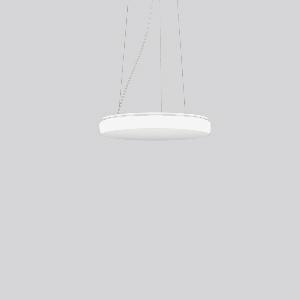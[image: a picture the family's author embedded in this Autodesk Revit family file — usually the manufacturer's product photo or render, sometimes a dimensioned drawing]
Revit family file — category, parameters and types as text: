
# Revit family: flat_polymero_kreis_slim_312090_002_4_76_7d1d
name_source: partatom
category: Lighting Fixtures
units: mm (PartAtom-declared; Revit-internal decimal feet)

## family parameters
Cut with Voids When Loaded = No
Host = Face
Light Source = No
Part Type = Normal
Room Calculation Point = No
Round Connector Dimension = Use Diameter
Shared = No

## types (1)
- FLAT POLYMERO KREIS SLIM (1 x LED Modul 840, 2200 lm, 4000)
    Apparent Load = 19 VA
    CIE Flux Codes = 44 75 94 92 100
    Color Rendering = 80
    Color Temperature = 4000
    Default Elevation = 1800 mm
    Description = Series: FLAT POLYMERO KREIS SLIM
Decorative round LED pendant luminaire. Base and canopy: metal, powder-coated, white. Canopy Ø 205 mm, h 35 mm. Diffuser made of plastic (polycarbonate), opal, shockproof. Diffuser fastening: patented push system. Homogeneous and smooth light distribution. Suitable for pendant. 3-point steel cable suspension, steplessly adjustable. Special lengths available on request. TouchDim sensor capable. Light and/or presence sensors can be integrated. 
Colour: white
Diameter: 460 mm
Height: 68 mm
Suspension length: 200-1300 mm
Lamp: LED
Socket: without socket
Colour temperature: 4000K
Colour rendering index (CRI): 80
System power: 19 W
Rated luminous flux: 2200 lm
Luminous efficiency: 116 lm/W
Control gear: AC power, DALI dimmable
Protection class: I
Type of protection: IP 40
    Height = 68 mm
    Lamp = 1 x LED Modul 840
    Lamp Light Flux = 2200 lm
    Lamp count = 1
    Length = 460 mm
    Lifetime = 50000 h
    Luminous efficacy = 116 lm/W
    Manufacturer = RZB
    ModVariant = No
    Model = 312090.002.4.76
    Mounting Place = Ceiling
    Mounting Type = Pendant
    Number of Poles = 1
    OnlyDefault = Yes
    Power Factor = 1
    Product Name = FLAT POLYMERO KREIS SLIM
    Product group = Pendant luminaires
    ProductGroupID = 902
    Protection Class = Protection class I
    Protection Degree = IP 40
    RLX_Detail_Level = 1
    RLX_Emergency_Light_Flux = 0 lm
    RLX_Emergency_Type = 0
    RLX_Emergency_Type_DB = No
    RlxData = <blob elided: 58237 chars, md5=c5b07f48>
    Socket = socket
    Standby Power = 0 W
    System Light Flux = 2200 lm
    System Power = 19 W
    Type Comments = Product without accessories
    Type Image = 312090.002.jpg
    URL = http://relux.com
    VarID = ---
    Voltage = 230 V
    Voltage Range = 220-240 V
    Weight = 0.00 kg
    Width = 0 mm  [stored 0 ft]

note: [stored X ft] marks values corroborated as IEEE doubles in the binary element streams (Revit-internal decimal feet)

## geometry (parser evidence)
native form markers: Blend x4, Sweep x13
no freeform markers — native parametric forms only
